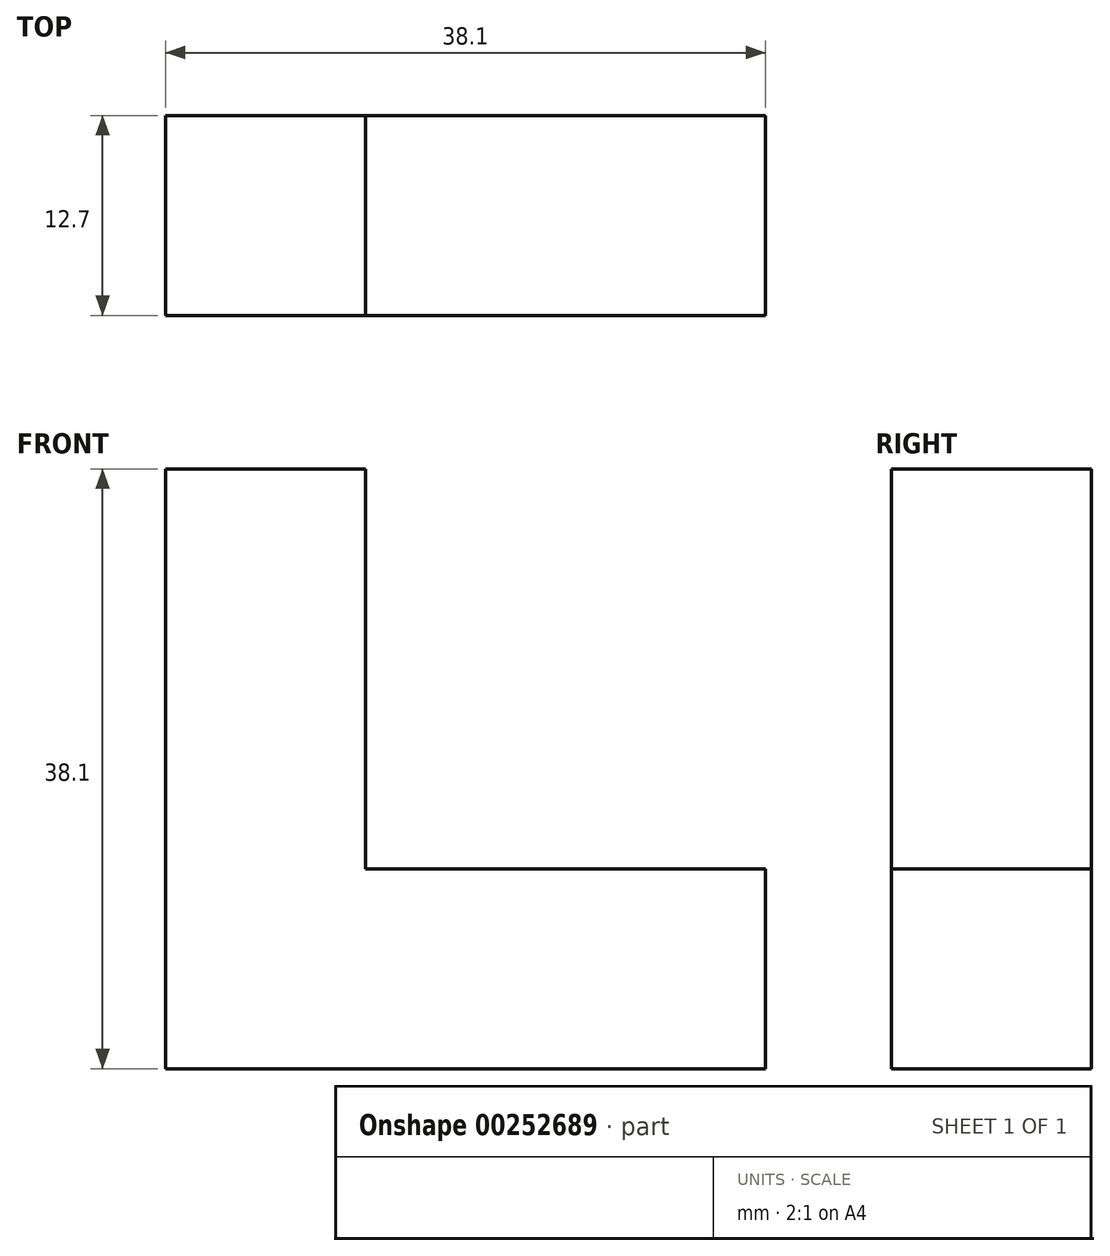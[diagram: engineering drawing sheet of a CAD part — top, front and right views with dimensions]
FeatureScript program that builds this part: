
annotation { "Feature Type Name" : "Feature", "Feature Type Description" : "" }
export const myFeature = defineFeature(function(context is Context, id is Id, definition is map)
    precondition{}
    {
        {
            var Q0;
            Q0=qCreatedBy(makeId("Front.planeOp"),FACE);
            var sketch = newSketch(context, id + "F0", { "sketchPlane" : qUnion([Q0])});
            skLineSegment(sketch, "E0", {"start": v(0, 0) * mm, "end": v(0, 38.1) * mm});
            skLineSegment(sketch, "E1", {"start": v(0, 0) * mm, "end": v(38.1, 0) * mm});
            skLineSegment(sketch, "E2", {"start": v(38.1, 0) * mm, "end": v(38.1, 12.7) * mm});
            skLineSegment(sketch, "E3", {"start": v(38.1, 12.7) * mm, "end": v(12.7, 12.7) * mm});
            skLineSegment(sketch, "E4", {"start": v(12.7, 12.7) * mm, "end": v(12.7, 38.1) * mm});
            skLineSegment(sketch, "E5", {"start": v(0, 38.1) * mm, "end": v(12.7, 38.1) * mm});
            skSolve(sketch);
        }
        {
            var Q0;
            Q0=makeQuery(id+"F0.imprint","IMPRINT",FACE,{"disambiguationData":[TD([[makeQuery(id+"F0.imprint","IMPRINT",EDGE,{"derivedFrom":sQuery(id+"F0.wireOp",EDGE,"E0")}),-1.0]])]});
            extrude(context, id + "F1", {"entities" : qUnion([Q0]), "depth" : 12.7 * mm});
        }
    });
